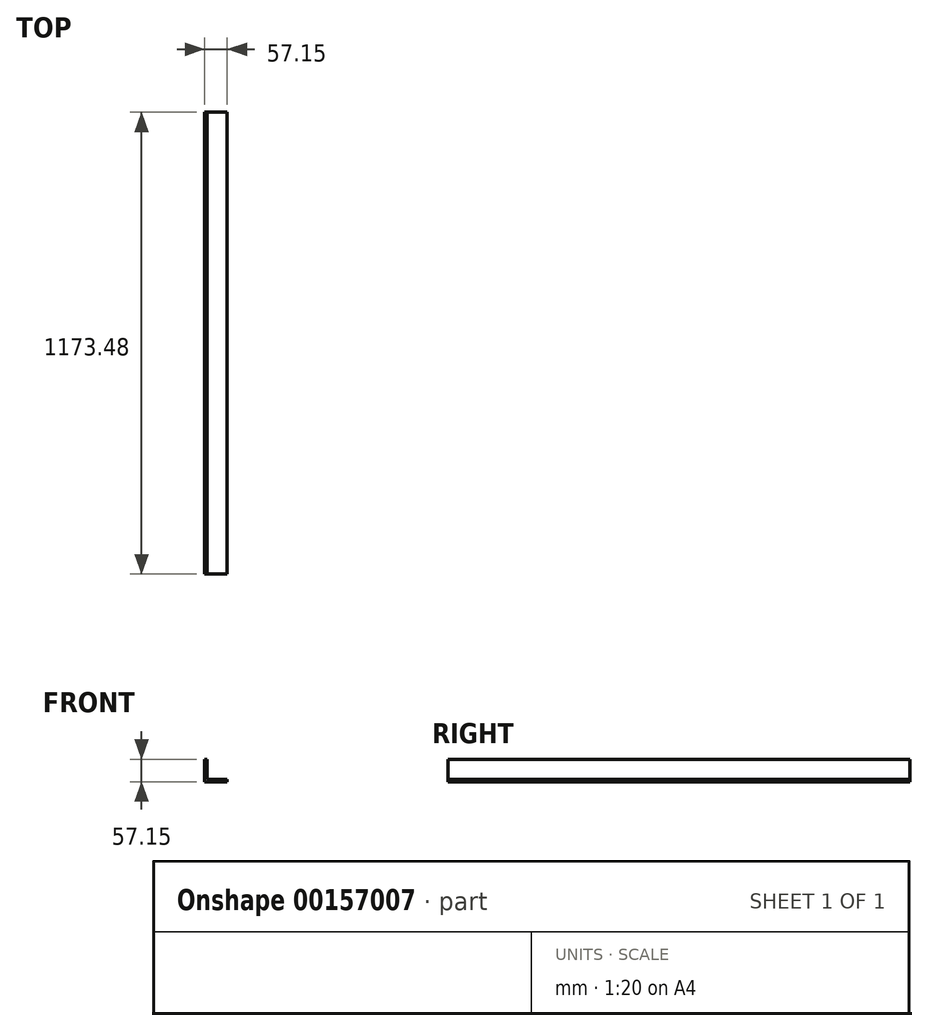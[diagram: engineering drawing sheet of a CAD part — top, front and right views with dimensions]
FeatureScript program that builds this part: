
annotation { "Feature Type Name" : "Feature", "Feature Type Description" : "" }
export const myFeature = defineFeature(function(context is Context, id is Id, definition is map)
    precondition{}
    {
        {
            var Q0;
            Q0=qCreatedBy(makeId("Front.planeOp"),FACE);
            var sketch = newSketch(context, id + "F0", { "sketchPlane" : qUnion([Q0])});
            skLineSegment(sketch, "E0", {"start": v(-15.55, 24.02) * mm, "end": v(-15.55, -26.78) * mm});
            skLineSegment(sketch, "E1", {"start": v(-15.55, -26.78) * mm, "end": v(35.25, -26.78) * mm});
            skLineSegment(sketch, "E2.0", {"start": v(-21.9, -33.13) * mm, "end": v(35.25, -33.13) * mm});
            skLineSegment(sketch, "E2.1", {"start": v(-21.9, 24.02) * mm, "end": v(-21.9, -33.13) * mm});
            skLineSegment(sketch, "E3", {"start": v(-21.9, 24.02) * mm, "end": v(-15.55, 24.02) * mm});
            skLineSegment(sketch, "E4", {"start": v(35.25, -26.78) * mm, "end": v(35.25, -33.13) * mm});
            skSolve(sketch);
        }
        {
            var Q0;
            Q0=makeQuery(id+"F0.imprint","IMPRINT",FACE,{"disambiguationData":[TD([[makeQuery(id+"F0.imprint","IMPRINT",EDGE,{"derivedFrom":sQuery(id+"F0.wireOp",EDGE,"E0")}),-1.0]])]});
            extrude(context, id + "F1", {"entities" : qUnion([Q0]), "depth" : 586.74 * mm});
        }
        {
            var Q0;
            Q0=makeQuery(id+"F1.opExtrude","CAP_FACE",FACE,{"disambiguationData":[OSD([sQuery(id+"F0.wireOp",EDGE,"E0"),sQuery(id+"F0.wireOp",EDGE,"E1"),sQuery(id+"F0.wireOp",EDGE,"E2.0"),sQuery(id+"F0.wireOp",EDGE,"E2.1"),sQuery(id+"F0.wireOp",EDGE,"E3"),sQuery(id+"F0.wireOp",EDGE,"E4")])],"isStart":true});
            extrude(context, id + "F2", {"entities" : qUnion([Q0]), "operationType" : NewBodyOperationType.ADD, "depth" : 586.74 * mm});
        }
    });
